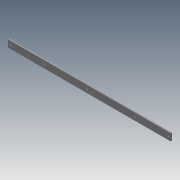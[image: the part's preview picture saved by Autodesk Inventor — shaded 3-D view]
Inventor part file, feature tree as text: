
AUTODESK INVENTOR PART (.ipt)
format: ipt  version: 2011 (Build 150239000, 239)  size: 140,288 bytes
history: native  units: in
note: dims shown in document units (in); Inventor stores cm internally (conversion verified against a paired STEP export)
features: extrude x10, sketch x10
ambient origin geometry x8: Origin, YZ Plane, XZ Plane, XY Plane, X Axis, Y Axis, Z Axis, Center Point
bodies: Solid1 (feature_tree)
feature tree (20):
  extrude  "Extrusion1"  Depth=0.5in
  extrude  "Extrusion2"  Depth=16.57in
  extrude  "Extrusion3"  Depth=0.156in
  extrude  "Extrusion4"  Depth=0.125in TaperAngle=0.0deg
  extrude  "Extrusion5"  Depth=3.765in
  extrude  "Extrusion6"  Depth=1.0in TaperAngle=0.0deg
  extrude  "Extrusion7"  Depth=0.125in TaperAngle=0.0deg
  extrude  "Extrusion8"  Depth=3.53in
  extrude  "Extrusion9"  Depth=0.125in TaperAngle=0.0deg
  extrude  "Extrusion10"  Depth=9.47in
  sketch  "Sketch1"  dims[d0=17.0in d1=0.5in]
  sketch  "Sketch2"  dims[d2=8.285in d3=16.57in]
  sketch  "Sketch3"  dims[d4=0.156in d5=0.156in]
  sketch  "Sketch4"  dims[d6=0.125in d7=0.0in d8=0.125in d9=0.0in]
  sketch  "Sketch5"  dims[d10=0.125in d11=0.0in d12=3.765in]
  sketch  "Sketch6"  dims[d13=3.765in d14=1.0in d15=0.0in]
  sketch  "Sketch7"  dims[d16=0.125in d17=0.0in d18=0.125in d19=0.0in]
  sketch  "Sketch8"  dims[d20=3.53in d21=3.53in]
  sketch  "Sketch9"  dims[d22=0.125in d23=0.0in d24=0.125in d25=0.0in]
  sketch  "Sketch10"  dims[d26=4.735in d27=9.47in d28=0.156in d29=3.53in d30=3.53in d31=0.125in d32=0.0in d33=0.25in d34=0.5in d35=0.125in d36=0.0in]
